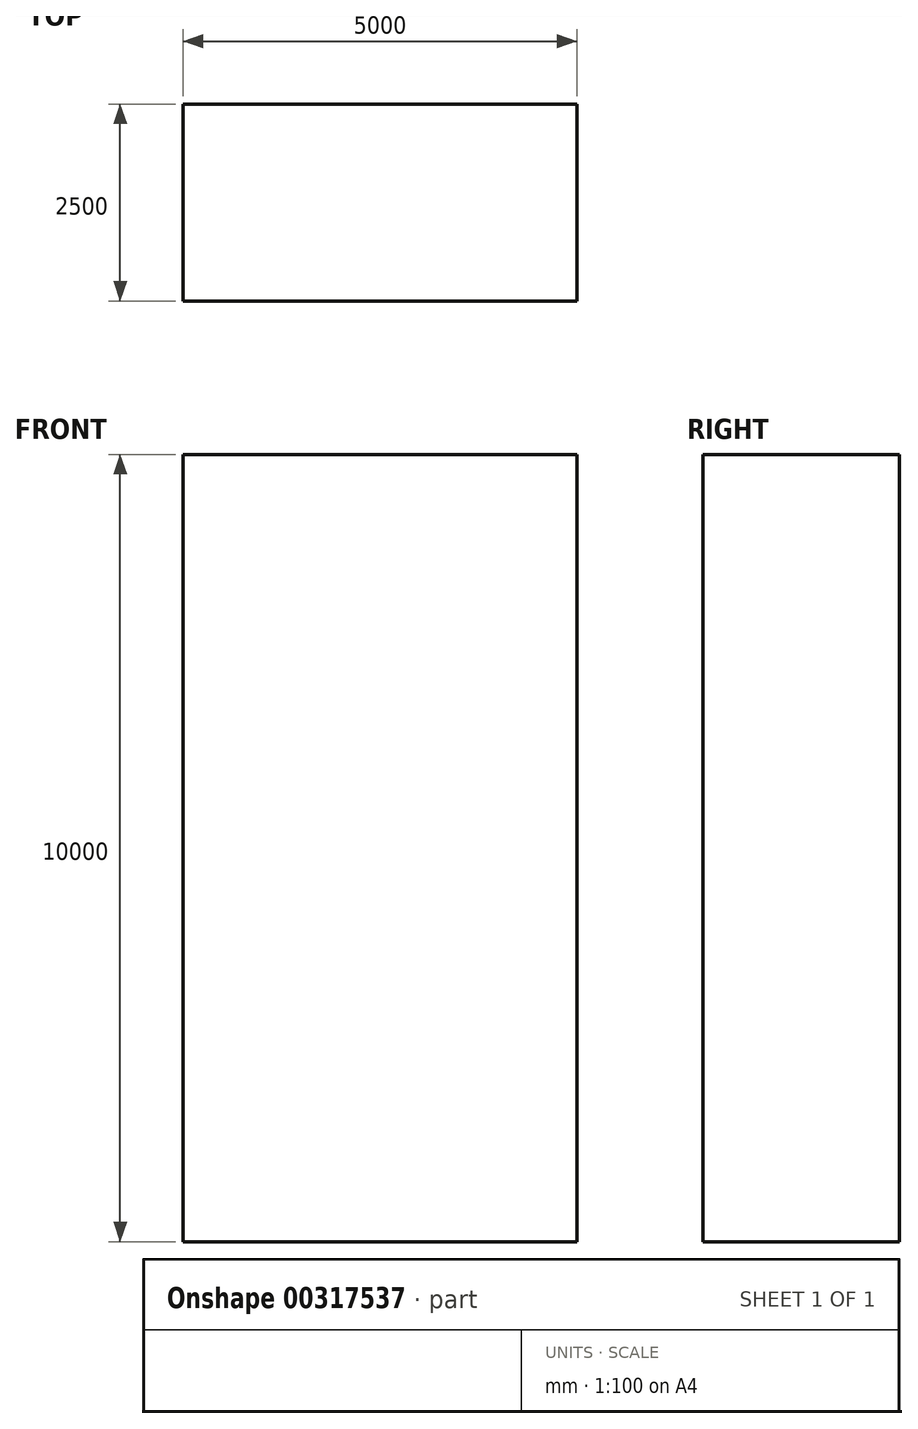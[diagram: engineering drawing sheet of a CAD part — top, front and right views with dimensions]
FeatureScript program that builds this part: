
annotation { "Feature Type Name" : "Feature", "Feature Type Description" : "" }
export const myFeature = defineFeature(function(context is Context, id is Id, definition is map)
    precondition{}
    {
        {
            var Q0;
            Q0=qCreatedBy(makeId("Front.planeOp"),FACE);
            var sketch = newSketch(context, id + "F0", { "sketchPlane" : qUnion([Q0])});
            skLineSegment(sketch, "E0", {"start": v(0, 0) * mm, "end": v(5000, 0) * mm});
            skLineSegment(sketch, "E1", {"start": v(5000, 0) * mm, "end": v(5000, 10000) * mm});
            skLineSegment(sketch, "E2", {"start": v(5000, 10000) * mm, "end": v(0, 10000) * mm});
            skLineSegment(sketch, "E3", {"start": v(0, 10000) * mm, "end": v(0, 0) * mm});
            skSolve(sketch);
        }
        {
            var Q0;
            Q0=makeQuery(id+"F0.imprint","IMPRINT",FACE,{"disambiguationData":[TD([[makeQuery(id+"F0.imprint","IMPRINT",EDGE,{"derivedFrom":sQuery(id+"F0.wireOp",EDGE,"E0")}),1.0]])]});
            extrude(context, id + "F1", {"entities" : qUnion([Q0]), "depth" : 2500 * mm});
        }
    });
